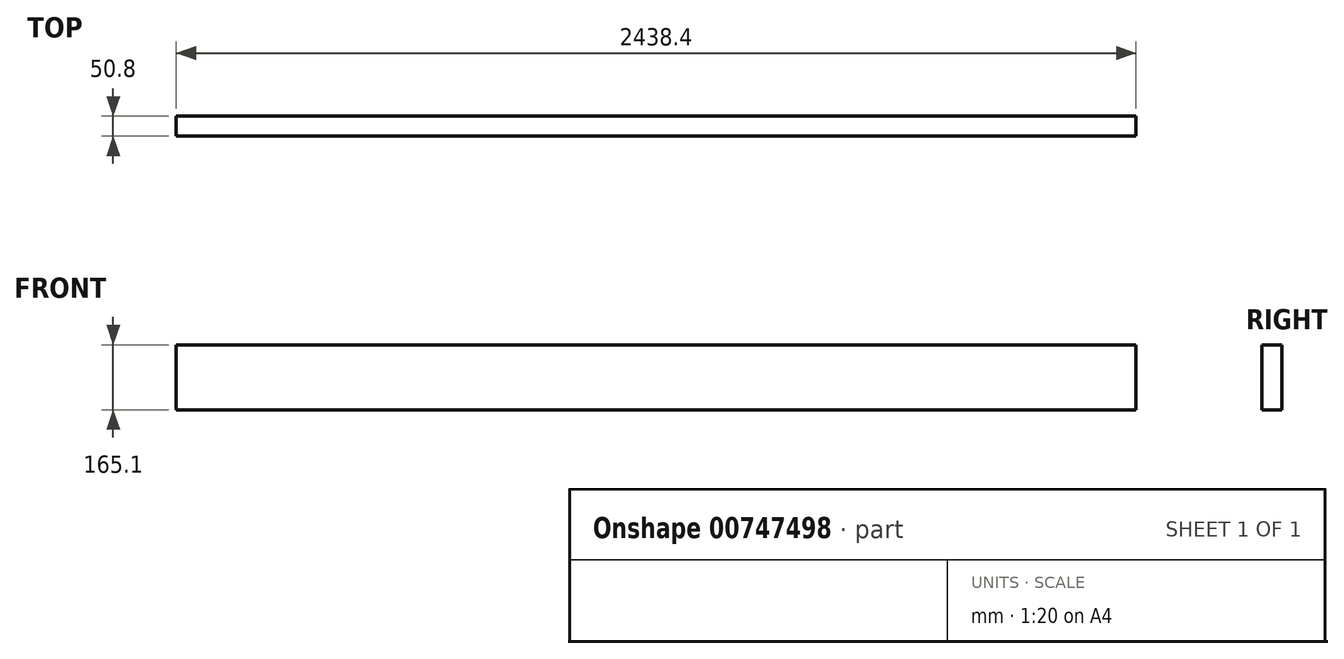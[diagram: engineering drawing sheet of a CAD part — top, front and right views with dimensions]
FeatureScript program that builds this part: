
annotation { "Feature Type Name" : "Feature", "Feature Type Description" : "" }
export const myFeature = defineFeature(function(context is Context, id is Id, definition is map)
    precondition{}
    {
        {
            var Q0;
            Q0=qCreatedBy(makeId("Front.planeOp"),FACE);
            var sketch = newSketch(context, id + "F0", { "sketchPlane" : qUnion([Q0])});
            skLineSegment(sketch, "E0.bottom", {"start": v(-385.61, 105.57) * mm, "end": v(2052.79, 105.57) * mm});
            skLineSegment(sketch, "E0.top", {"start": v(-385.61, -59.53) * mm, "end": v(2052.79, -59.53) * mm});
            skLineSegment(sketch, "E0.left", {"start": v(-385.61, 105.57) * mm, "end": v(-385.61, -59.53) * mm});
            skLineSegment(sketch, "E0.right", {"start": v(2052.79, 105.57) * mm, "end": v(2052.79, -59.53) * mm});
            skSolve(sketch);
        }
        {
            var Q0;
            Q0=makeQuery(id+"F0.imprint","IMPRINT",FACE,{"disambiguationData":[TD([[makeQuery(id+"F0.imprint","IMPRINT",EDGE,{"derivedFrom":sQuery(id+"F0.wireOp",EDGE,"E0.bottom")}),-1.0]])]});
            extrude(context, id + "F1", {"entities" : qUnion([Q0]), "depth" : 50.8 * mm, "offsetDistance" : 25.4 * mm});
        }
    });
